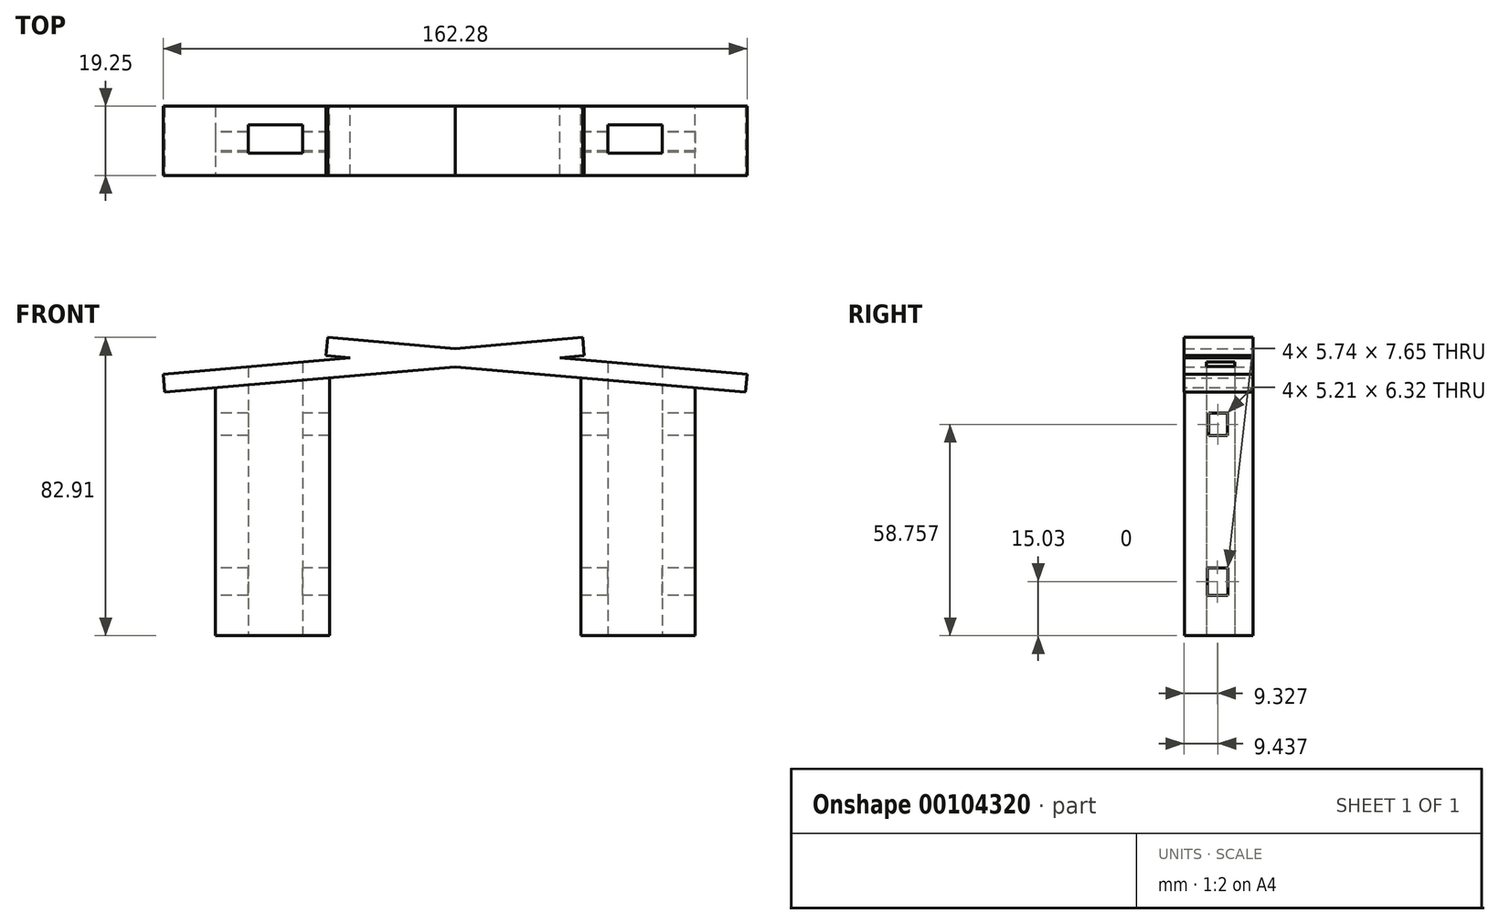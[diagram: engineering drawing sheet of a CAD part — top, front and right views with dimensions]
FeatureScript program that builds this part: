
annotation { "Feature Type Name" : "Feature", "Feature Type Description" : "" }
export const myFeature = defineFeature(function(context is Context, id is Id, definition is map)
    precondition{}
    {
        {
            var Q0;
            Q0=qCreatedBy(makeId("Top.planeOp"),FACE);
            var sketch = newSketch(context, id + "F0", { "sketchPlane" : qUnion([Q0])});
            skLineSegment(sketch, "E0.bottom", {"start": v(-41.3, 0) * mm, "end": v(-34.96, 0) * mm});
            skLineSegment(sketch, "E0.top", {"start": v(-41.3, -6.35) * mm, "end": v(-34.96, -6.35) * mm});
            skLineSegment(sketch, "E0.left", {"start": v(-41.3, 0) * mm, "end": v(-41.3, -6.35) * mm});
            skLineSegment(sketch, "E0.right", {"start": v(-34.96, 0) * mm, "end": v(-34.96, -6.35) * mm});
            skLineSegment(sketch, "E1.bottom", {"start": v(-64.57, 0) * mm, "end": v(-45.06, 0) * mm});
            skLineSegment(sketch, "E1.top", {"start": v(-64.57, -6.35) * mm, "end": v(-45.06, -6.35) * mm});
            skLineSegment(sketch, "E1.left", {"start": v(-64.57, 0) * mm, "end": v(-64.57, -6.35) * mm});
            skLineSegment(sketch, "E1.right", {"start": v(-45.06, 0) * mm, "end": v(-45.06, -6.35) * mm});
            skSolve(sketch);
        }
        {
            var Q0;
            Q0=makeQuery(id+"F0.imprint","IMPRINT",FACE,{"disambiguationData":[TD([[makeQuery(id+"F0.imprint","IMPRINT",EDGE,{"derivedFrom":sQuery(id+"F0.wireOp",EDGE,"E0.bottom")}),-1.0]])]});
            extrude(context, id + "F1", {"entities" : qUnion([Q0]), "depth" : 76.2 * mm});
        }
        {
            var Q0;
            Q0=makeQuery(id+"F1.opExtrude","CAP_EDGE",EDGE,{"disambiguationData":[OSD([sQuery(id+"F0.wireOp",EDGE,"E0.left")])],"isStart":false});
            cPlane(context, id + "F2", {"entities" : qUnion([Q0]), "cplaneType" : CPlaneType.LINE_ANGLE, "offset" : 25.4 * mm, "angle" : 5 * degree, "width" : 152.4 * mm, "height" : 152.4 * mm});
        }
        {
            var Q0;
            Q0=qCreatedBy(id+"F2.planeOp",FACE);
            var sketch = newSketch(context, id + "F3", { "sketchPlane" : qUnion([Q0])});
            skLineSegment(sketch, "E2.bottom", {"start": v(-36.4, 0) * mm, "end": v(42.53, 0) * mm});
            skLineSegment(sketch, "E2.top", {"start": v(-36.4, 6.55) * mm, "end": v(42.53, 6.55) * mm});
            skLineSegment(sketch, "E2.left", {"start": v(-36.4, 0) * mm, "end": v(-36.4, 6.55) * mm});
            skLineSegment(sketch, "E2.right", {"start": v(42.53, 0) * mm, "end": v(42.53, 6.55) * mm});
            skSolve(sketch);
        }
        {
            var Q0;
            Q0=makeQuery(id+"F3.imprint","IMPRINT",FACE,{"disambiguationData":[TD([[makeQuery(id+"F3.imprint","IMPRINT",EDGE,{"derivedFrom":sQuery(id+"F3.wireOp",EDGE,"E2.bottom")}),1.0]])]});
            extrude(context, id + "F4", {"entities" : qUnion([Q0]), "operationType" : NewBodyOperationType.ADD, "depth" : 5.08 * mm});
        }
        {
            var Q0;
            Q0=makeQuery(id+"F4.opExtrude","SWEPT_FACE",FACE,{"disambiguationData":[OSD([sQuery(id+"F3.wireOp",EDGE,"E2.left")])]});
            extrude(context, id + "F5", {"entities" : qUnion([Q0]), "operationType" : NewBodyOperationType.ADD, "depth" : 38.1 * mm});
        }
        {
            var Q0;
            Q0=makeQuery(id+"F1.opExtrude","SWEPT_BODY",BODY,{"disambiguationData":[OSD([sQuery(id+"F0.wireOp",EDGE,"E0.bottom"),sQuery(id+"F0.wireOp",EDGE,"E0.top"),sQuery(id+"F0.wireOp",EDGE,"E0.left"),sQuery(id+"F0.wireOp",EDGE,"E0.right")])]});
            var Q1;
            Q1=makeQuery(id+"FoHI6DNbYifgutx_0.opExtrude","SWEPT_BODY",BODY,{"disambiguationData":[OSD([sQuery(id+"F0.wireOp",EDGE,"E1.bottom"),sQuery(id+"F0.wireOp",EDGE,"E1.top"),sQuery(id+"F0.wireOp",EDGE,"E1.left"),sQuery(id+"F0.wireOp",EDGE,"E1.right")])]});
            var Q2;
            Q2=qCreatedBy(makeId("Right.planeOp"),FACE);
            mirror(context, id + "F6", {"operationType" : NewBodyOperationType.ADD, "entities" : qUnion([Q0, Q1]), "mirrorPlane" : qUnion([Q2])});
        }
        {
            var Q0;
            Q0=makeQuery(id+"F1.opExtrude","SWEPT_FACE",FACE,{"disambiguationData":[OSD([sQuery(id+"F0.wireOp",EDGE,"E0.left")])]});
            extrude(context, id + "F7", {"entities" : qUnion([Q0]), "operationType" : NewBodyOperationType.ADD, "depth" : 25.4 * mm});
        }
        {
            var Q0;
            Q0=makeQuery(id+"F6.opPattern","COPY",FACE,{"derivedFrom":makeQuery(id+"F1.opExtrude","SWEPT_FACE",FACE,{"disambiguationData":[OSD([sQuery(id+"F0.wireOp",EDGE,"E0.left")])]}),"instanceName":"1"});
            extrude(context, id + "F8", {"entities" : qUnion([Q0]), "operationType" : NewBodyOperationType.ADD, "depth" : 25.4 * mm});
        }
        {
            var Q0;
            {var subQ0=sQuery(id+"F3.wireOp",EDGE,"E2.top");var subQ1=makeQuery(id+"F5.boolean.opBoolean","MERGE",FACE,{"derivedFrom":[makeQuery(id+"F4.opExtrude","SWEPT_FACE",FACE,{"disambiguationData":[OSD([subQ0])]}),makeQuery(id+"F5.opExtrude","SWEPT_FACE",FACE,{"disambiguationData":[OSD([subQ0,sQuery(id+"F3.wireOp",EDGE,"E2.left")])]})]});Q0=makeQuery(id+"F6.boolean.opBoolean","MERGE",FACE,{"derivedFrom":[subQ1,makeQuery(id+"F6.opPattern","COPY",FACE,{"derivedFrom":subQ1,"instanceName":"1"})]});}
            extrude(context, id + "F9", {"entities" : qUnion([Q0]), "operationType" : NewBodyOperationType.ADD, "depth" : 12.7 * mm});
        }
        {
            var Q0;
            {var subQ0=sQuery(id+"F0.wireOp",EDGE,"E0.top");Q0=makeQuery(id+"F7.boolean.opBoolean","MERGE",FACE,{"derivedFrom":[makeQuery(id+"F1.opExtrude","SWEPT_FACE",FACE,{"disambiguationData":[OSD([subQ0])]}),makeQuery(id+"F7.opExtrude","SWEPT_FACE",FACE,{"disambiguationData":[OSD([subQ0,sQuery(id+"F0.wireOp",EDGE,"E0.left")])]})]});}
            var Q1;
            {var subQ0=sQuery(id+"F0.wireOp",EDGE,"E0.top");Q1=makeQuery(id+"F8.boolean.opBoolean","MERGE",FACE,{"derivedFrom":[makeQuery(id+"F6.opPattern","COPY",FACE,{"derivedFrom":makeQuery(id+"F1.opExtrude","SWEPT_FACE",FACE,{"disambiguationData":[OSD([subQ0])]}),"instanceName":"1"}),makeQuery(id+"F8.opExtrude","SWEPT_FACE",FACE,{"disambiguationData":[OSD([subQ0,sQuery(id+"F0.wireOp",EDGE,"E0.left")])]})]});}
            extrude(context, id + "F10", {"entities" : qUnion([Q0, Q1]), "operationType" : NewBodyOperationType.ADD, "depth" : 12.7 * mm});
        }
        {
            var Q0;
            {var subQ0=sQuery(id+"F0.wireOp",EDGE,"E0.left");var subQ1=sQuery(id+"F0.wireOp",EDGE,"E0.top");Q0=makeQuery(id+"F10.boolean.opBoolean","MERGE",FACE,{"derivedFrom":[makeQuery(id+"F7.boolean.opBoolean","MERGE",FACE,{"derivedFrom":[makeQuery(id+"F1.opExtrude","CAP_FACE",FACE,{"disambiguationData":[OSD([sQuery(id+"F0.wireOp",EDGE,"E0.bottom"),subQ1,subQ0,sQuery(id+"F0.wireOp",EDGE,"E0.right")])],"isStart":true}),makeQuery(id+"F7.opExtrude","SWEPT_FACE",FACE,{"disambiguationData":[OSD([subQ0])]})]}),makeQuery(id+"F10.opExtrude","SWEPT_FACE",FACE,{"disambiguationData":[OSD([subQ1,subQ0]),TDD([makeQuery(id+"F7.boolean.opBoolean","MERGE",EDGE,{"derivedFrom":[makeQuery(id+"F1.opExtrude","CAP_EDGE",EDGE,{"disambiguationData":[OSD([subQ1])],"isStart":true}),makeQuery(id+"F7.opExtrude","SWEPT_EDGE",EDGE,{"disambiguationData":[OSD([subQ1,subQ0])]})]})])]})]});}
            var sketch = newSketch(context, id + "F11", { "sketchPlane" : qUnion([Q0])});
            skLineSegment(sketch, "E3.bottom", {"start": v(-57.5, 13) * mm, "end": v(-42.44, 13) * mm});
            skLineSegment(sketch, "E3.top", {"start": v(-57.5, 5.12) * mm, "end": v(-42.44, 5.12) * mm});
            skLineSegment(sketch, "E3.left", {"start": v(-57.5, 13) * mm, "end": v(-57.5, 5.12) * mm});
            skLineSegment(sketch, "E3.right", {"start": v(-42.44, 13) * mm, "end": v(-42.44, 5.12) * mm});
            skLineSegment(sketch, "E4.MirrorCS", {"start": v(42.44, 13) * mm, "end": v(42.44, 5.12) * mm});
            skLineSegment(sketch, "E5.MirrorCS", {"start": v(57.5, 5.12) * mm, "end": v(42.44, 5.12) * mm});
            skLineSegment(sketch, "E6.MirrorCS", {"start": v(57.5, 13) * mm, "end": v(57.5, 5.12) * mm});
            skLineSegment(sketch, "E7.MirrorCS", {"start": v(57.5, 13) * mm, "end": v(42.44, 13) * mm});
            skSolve(sketch);
        }
        {
            var Q0;
            Q0 = qSketchRegion(id + "F11", true);
            extrude(context, id + "F12", {"entities" : qUnion([Q0]), "operationType" : NewBodyOperationType.REMOVE, "oppositeDirection" : true, "depth" : 88.9 * mm});
        }
        {
            var Q0;
            {var subQ4=sQuery(id+"F0.wireOp",EDGE,"E0.top");var subQ5=makeQuery(id+"F1.opExtrude","SWEPT_FACE",FACE,{"disambiguationData":[OSD([subQ4])]});var subQ6=sQuery(id+"F0.wireOp",EDGE,"E0.left");var subQ11=makeQuery(id+"F7.opExtrude","CAP_FACE",FACE,{"disambiguationData":[OSD([subQ6])],"isStart":false});Q0=makeQuery(id+"F10.boolean.opBoolean","MERGE",FACE,{"derivedFrom":[makeQuery(id+"F7.boolean.opBoolean","SPLIT",FACE,{"disambiguationData":[TD([subQ5])],"derivedFrom":subQ11}),makeQuery(id+"F10.opExtrude","SWEPT_FACE",FACE,{"disambiguationData":[OSD([subQ4,subQ6]),TDD([makeQuery(id+"F7.boolean.opBoolean","SPLIT",EDGE,{"disambiguationData":[TD([subQ5])],"derivedFrom":makeQuery(id+"F7.opExtrude","CAP_EDGE",EDGE,{"disambiguationData":[OSD([subQ4,subQ6])],"isStart":false})})])]})]});}
            var sketch = newSketch(context, id + "F13", { "sketchPlane" : qUnion([Q0])});
            skLineSegment(sketch, "E8.bottom", {"start": v(7.05, 76.06) * mm, "end": v(12.8, 76.06) * mm});
            skLineSegment(sketch, "E8.top", {"start": v(7.05, 68.4) * mm, "end": v(12.8, 68.4) * mm});
            skLineSegment(sketch, "E8.left", {"start": v(7.05, 76.06) * mm, "end": v(7.05, 68.4) * mm});
            skLineSegment(sketch, "E8.right", {"start": v(12.8, 76.06) * mm, "end": v(12.8, 68.4) * mm});
            skLineSegment(sketch, "E9.bottom", {"start": v(7.05, 11.2) * mm, "end": v(12.8, 11.2) * mm});
            skLineSegment(sketch, "E9.top", {"start": v(7.05, 18.85) * mm, "end": v(12.8, 18.85) * mm});
            skLineSegment(sketch, "E9.left", {"start": v(7.05, 11.2) * mm, "end": v(7.05, 18.85) * mm});
            skLineSegment(sketch, "E9.right", {"start": v(12.8, 11.2) * mm, "end": v(12.8, 18.85) * mm});
            skSolve(sketch);
        }
        {
            var Q0;
            Q0=makeQuery(id+"F13.imprint","IMPRINT",FACE,{"disambiguationData":[TD([[makeQuery(id+"F13.imprint","IMPRINT",EDGE,{"derivedFrom":sQuery(id+"F13.wireOp",EDGE,"E9.bottom")}),1.0]])]});
            extrude(context, id + "F14", {"entities" : qUnion([Q0]), "operationType" : NewBodyOperationType.REMOVE, "oppositeDirection" : true, "depth" : 2540 * mm});
        }
        {
            var Q0;
            {var subQ0=sQuery(id+"F0.wireOp",EDGE,"E0.left");var subQ1=sQuery(id+"F0.wireOp",EDGE,"E0.top");Q0=makeQuery(id+"F10.boolean.opBoolean","MERGE",FACE,{"derivedFrom":[makeQuery(id+"F7.opExtrude","CAP_FACE",FACE,{"disambiguationData":[OSD([subQ0])],"isStart":false}),makeQuery(id+"F10.opExtrude","SWEPT_FACE",FACE,{"disambiguationData":[OSD([subQ1,subQ0]),TDD([makeQuery(id+"F7.opExtrude","CAP_EDGE",EDGE,{"disambiguationData":[OSD([subQ1,subQ0])],"isStart":false})])]})]});}
            var sketch = newSketch(context, id + "F15", { "sketchPlane" : qUnion([Q0])});
            skLineSegment(sketch, "E10.bottom", {"start": v(7.2, 61.92) * mm, "end": v(12.42, 61.92) * mm});
            skLineSegment(sketch, "E10.top", {"start": v(7.2, 55.6) * mm, "end": v(12.42, 55.6) * mm});
            skLineSegment(sketch, "E10.left", {"start": v(7.2, 61.92) * mm, "end": v(7.2, 55.6) * mm});
            skLineSegment(sketch, "E10.right", {"start": v(12.42, 61.92) * mm, "end": v(12.42, 55.6) * mm});
            skSolve(sketch);
        }
        {
            var Q0;
            Q0=makeQuery(id+"F15.imprint","IMPRINT",FACE,{"disambiguationData":[TD([[makeQuery(id+"F15.imprint","IMPRINT",EDGE,{"derivedFrom":sQuery(id+"F15.wireOp",EDGE,"E10.bottom")}),-1.0]])]});
            extrude(context, id + "F16", {"entities" : qUnion([Q0]), "operationType" : NewBodyOperationType.REMOVE, "oppositeDirection" : true, "depth" : 25400 * mm});
        }
    });
